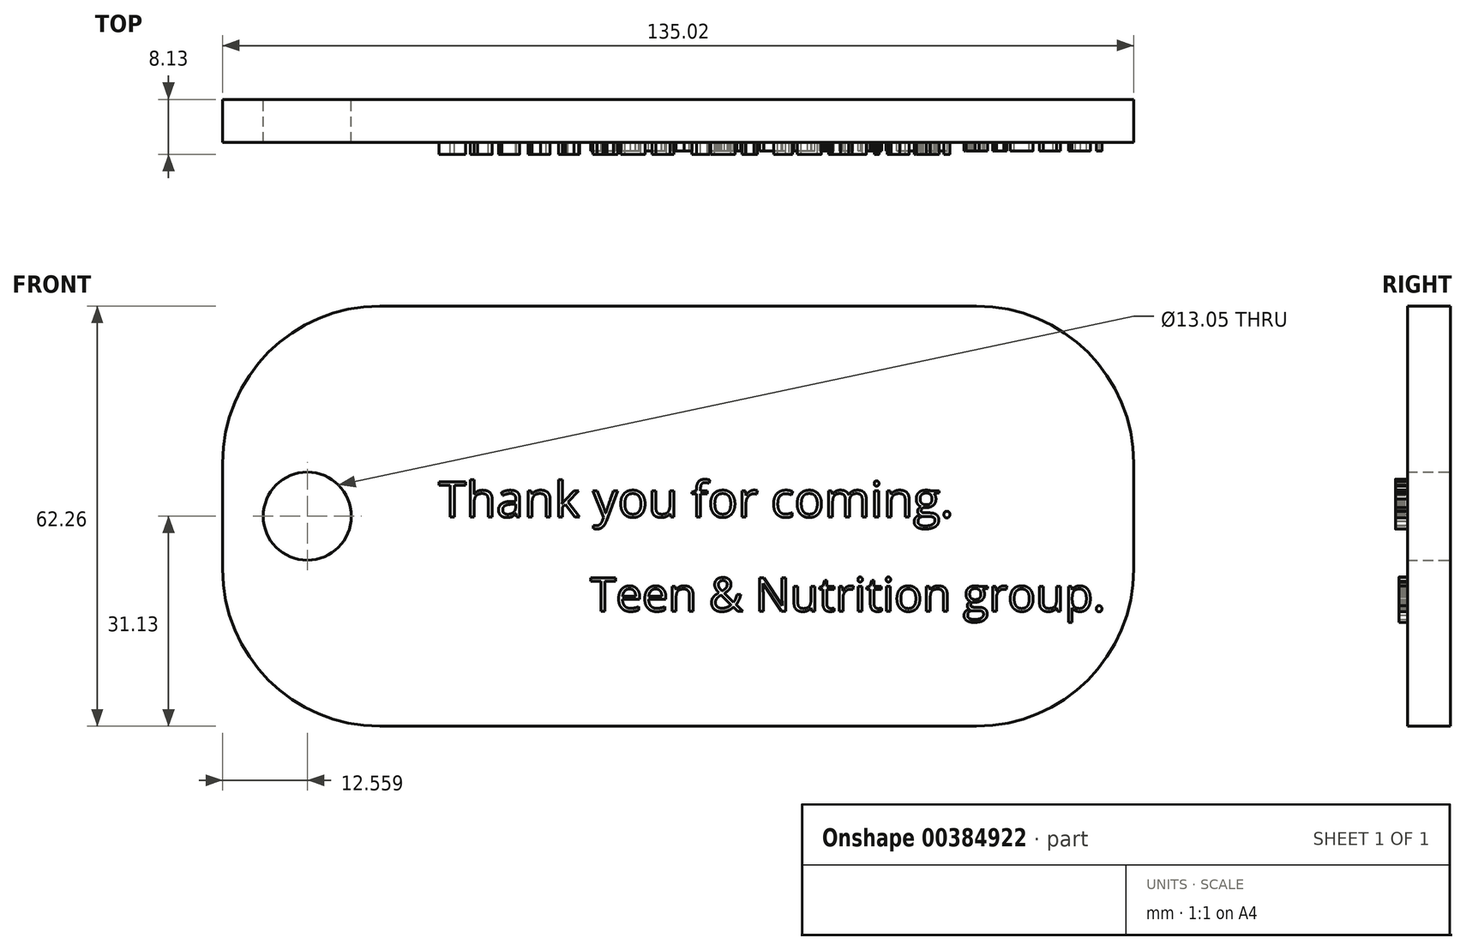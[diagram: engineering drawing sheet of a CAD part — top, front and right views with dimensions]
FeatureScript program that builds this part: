
annotation { "Feature Type Name" : "Feature", "Feature Type Description" : "" }
export const myFeature = defineFeature(function(context is Context, id is Id, definition is map)
    precondition{}
    {
        {
            var Q0;
            Q0=qCreatedBy(makeId("Front.planeOp"),FACE);
            var sketch = newSketch(context, id + "F0", { "sketchPlane" : qUnion([Q0])});
            skLineSegment(sketch, "E0.bottom", {"start": v(67.5, 31.13) * mm, "end": v(-67.5, 31.13) * mm});
            skLineSegment(sketch, "E0.top", {"start": v(67.5, -31.13) * mm, "end": v(-67.5, -31.13) * mm});
            skLineSegment(sketch, "E0.left", {"start": v(67.5, 31.13) * mm, "end": v(67.5, -31.13) * mm});
            skLineSegment(sketch, "E0.right", {"start": v(-67.5, 31.13) * mm, "end": v(-67.5, -31.13) * mm});
            skPoint(sketch, "E0.middle", {"position": v(0, 0) * mm});
            skSolve(sketch);
        }
        {
            var Q0;
            Q0=makeQuery(id+"F0.imprint","IMPRINT",FACE,{"disambiguationData":[TD([[makeQuery(id+"F0.imprint","IMPRINT",EDGE,{"derivedFrom":sQuery(id+"F0.wireOp",EDGE,"E0.bottom")}),1.0]])]});
            extrude(context, id + "F1", {"entities" : qUnion([Q0]), "endBound" : BoundingType.SYMMETRIC, "depth" : 6.35 * mm});
        }
        {
            var Q0;
            Q0=makeQuery(id+"F1.opExtrude","SWEPT_EDGE",EDGE,{"disambiguationData":[OSD([sQuery(id+"F0.wireOp",EDGE,"E0.bottom"),sQuery(id+"F0.wireOp",EDGE,"E0.right")])]});
            var Q1;
            Q1=makeQuery(id+"F1.opExtrude","SWEPT_EDGE",EDGE,{"disambiguationData":[OSD([sQuery(id+"F0.wireOp",EDGE,"E0.top"),sQuery(id+"F0.wireOp",EDGE,"E0.left")])]});
            var Q2;
            Q2=makeQuery(id+"F1.opExtrude","SWEPT_EDGE",EDGE,{"disambiguationData":[OSD([sQuery(id+"F0.wireOp",EDGE,"E0.bottom"),sQuery(id+"F0.wireOp",EDGE,"E0.left")])]});
            var Q3;
            Q3=makeQuery(id+"F1.opExtrude","SWEPT_EDGE",EDGE,{"disambiguationData":[OSD([sQuery(id+"F0.wireOp",EDGE,"E0.top"),sQuery(id+"F0.wireOp",EDGE,"E0.right")])]});
            fillet(context, id + "F2", {"entities" : qUnion([Q0, Q1, Q2, Q3]), "radius" : 23.3 * mm, "tangentPropagation" : true, "allowEdgeOverflow" : false});
        }
        {
            var Q0;
            Q0=qCreatedBy(makeId("Front.planeOp"),FACE);
            var sketch = newSketch(context, id + "F3", { "sketchPlane" : qUnion([Q0])});
            skCircle(sketch, "E1", {"center": v(-54.95, 0) * mm, "radius": 6.52 * mm});
            skSolve(sketch);
        }
        {
            var Q0;
            Q0 = qSketchRegion(id + "F3", true);
            extrude(context, id + "F4", {"entities" : qUnion([Q0]), "operationType" : NewBodyOperationType.REMOVE, "endBound" : BoundingType.SYMMETRIC, "depth" : 25.4 * mm});
        }
        {
            var Q0;
            Q0=makeQuery(id+"F1.opExtrude","CAP_FACE",FACE,{"disambiguationData":[OSD([sQuery(id+"F0.wireOp",EDGE,"E0.bottom"),sQuery(id+"F0.wireOp",EDGE,"E0.top"),sQuery(id+"F0.wireOp",EDGE,"E0.left"),sQuery(id+"F0.wireOp",EDGE,"E0.right")])],"isStart":false});
            var sketch = newSketch(context, id + "F5", { "sketchPlane" : qUnion([Q0])});
            skText(sketch, "E2", { "text": "Thank you for coming.", "fontName": "OpenSans-Regular.ttf"});
            const initialGuessF5  = {"E2": [-0.03551, -0.00014, 1, 0, 0.00528]};
            skSetInitialGuess(sketch, initialGuessF5);
            skSolve(sketch);
        }
        {
            var Q0;
            Q0 = qSketchRegion(id + "F5", true);
            extrude(context, id + "F6", {"entities" : qUnion([Q0]), "operationType" : NewBodyOperationType.ADD, "depth" : 1.78 * mm});
        }
        {
            var Q0;
            {var subQ0=sQuery(id+"F0.wireOp",EDGE,"E0.right");var subQ1=sQuery(id+"F0.wireOp",EDGE,"E0.left");var subQ2=sQuery(id+"F0.wireOp",EDGE,"E0.top");var subQ3=sQuery(id+"F0.wireOp",EDGE,"E0.bottom");Q0=makeQuery(id+"F6.boolean.opBoolean","SPLIT",FACE,{"disambiguationData":[TD([makeQuery(id+"F1.opExtrude","SWEPT_FACE",FACE,{"disambiguationData":[OSD([subQ3])]})])],"derivedFrom":makeQuery(id+"F1.opExtrude","CAP_FACE",FACE,{"disambiguationData":[OSD([subQ3,subQ2,subQ1,subQ0])],"isStart":false})});}
            var sketch = newSketch(context, id + "F7", { "sketchPlane" : qUnion([Q0])});
            skText(sketch, "E3", { "text": "Teen & Nutrition group.", "fontName": "OpenSans-Regular.ttf"});
            const initialGuessF7  = {"E3": [-0.01303, -0.01408, 1, 0, 0.00497]};
            skSetInitialGuess(sketch, initialGuessF7);
            skSolve(sketch);
        }
        {
            var Q0;
            Q0 = qSketchRegion(id + "F7", true);
            extrude(context, id + "F8", {"entities" : qUnion([Q0]), "operationType" : NewBodyOperationType.ADD, "depth" : 1.27 * mm});
        }
    });
